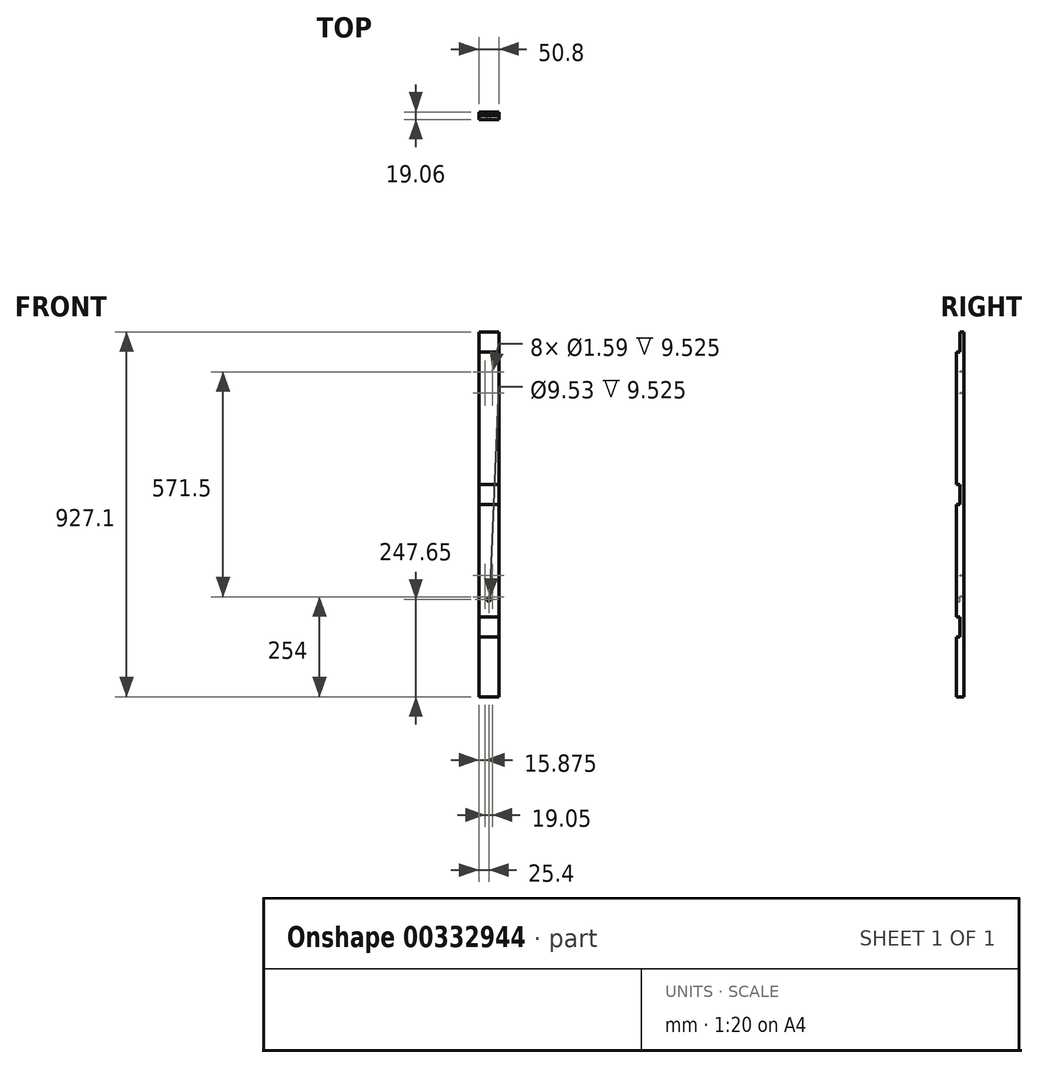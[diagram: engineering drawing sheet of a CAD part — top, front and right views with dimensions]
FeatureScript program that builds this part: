
annotation { "Feature Type Name" : "Feature", "Feature Type Description" : "" }
export const myFeature = defineFeature(function(context is Context, id is Id, definition is map)
    precondition{}
    {
        {
            var Q0;
            Q0=qCreatedBy(makeId("Top.planeOp"),FACE);
            var sketch = newSketch(context, id + "F0", { "sketchPlane" : qUnion([Q0])});
            skLineSegment(sketch, "E0.bottom", {"start": v(25.4, 9.53) * mm, "end": v(-25.4, 9.53) * mm});
            skLineSegment(sketch, "E0.top", {"start": v(25.4, -9.53) * mm, "end": v(-25.4, -9.53) * mm});
            skLineSegment(sketch, "E0.left", {"start": v(25.4, 9.53) * mm, "end": v(25.4, -9.52) * mm});
            skLineSegment(sketch, "E0.right", {"start": v(-25.4, 9.53) * mm, "end": v(-25.4, -9.53) * mm});
            skPoint(sketch, "E0.middle", {"position": v(0, 0) * mm});
            skSolve(sketch);
        }
        {
            var Q0;
            Q0=makeQuery(id+"F0.imprint","IMPRINT",FACE,{"disambiguationData":[TD([[makeQuery(id+"F0.imprint","IMPRINT",EDGE,{"derivedFrom":sQuery(id+"F0.wireOp",EDGE,"E0.bottom")}),1.0]])]});
            var Q1;
            Q1 = qSketchRegion(id + "F2", true);
            extrude(context, id + "F1", {"entities" : qUnion([Q0, Q1]), "depth" : 927.1 * mm});
        }
        {
            var Q0;
            Q0=qCreatedBy(makeId("Front.planeOp"),FACE);
            var sketch = newSketch(context, id + "F2", { "sketchPlane" : qUnion([Q0])});
            skLineSegment(sketch, "E1.bottom", {"start": v(-38.77, 152.4) * mm, "end": v(83.66, 152.4) * mm});
            skLineSegment(sketch, "E1.top", {"start": v(-38.77, 203.2) * mm, "end": v(83.66, 203.2) * mm});
            skLineSegment(sketch, "E1.left", {"start": v(-38.77, 152.4) * mm, "end": v(-38.77, 203.2) * mm});
            skLineSegment(sketch, "E1.right", {"start": v(83.66, 152.4) * mm, "end": v(83.66, 203.2) * mm});
            skLineSegment(sketch, "E2.bottom", {"start": v(-210.36, 876.3) * mm, "end": v(132.8, 876.3) * mm});
            skLineSegment(sketch, "E2.top", {"start": v(-210.36, 927.1) * mm, "end": v(132.8, 927.1) * mm});
            skLineSegment(sketch, "E2.left", {"start": v(-210.36, 876.3) * mm, "end": v(-210.36, 927.1) * mm});
            skLineSegment(sketch, "E2.right", {"start": v(132.8, 876.3) * mm, "end": v(132.8, 927.1) * mm});
            skLineSegment(sketch, "E3.bottom", {"start": v(-179.92, 539.75) * mm, "end": v(84.62, 539.75) * mm});
            skLineSegment(sketch, "E3.top", {"start": v(-179.92, 488.95) * mm, "end": v(84.62, 488.95) * mm});
            skLineSegment(sketch, "E3.left", {"start": v(-179.92, 539.75) * mm, "end": v(-179.92, 488.95) * mm});
            skLineSegment(sketch, "E3.right", {"start": v(84.62, 539.75) * mm, "end": v(84.62, 488.95) * mm});
            skSolve(sketch);
        }
        {
            var Q0;
            Q0=qSketchRegion(id+"F2",true);
            extrude(context, id + "F3", {"entities" : qUnion([Q0]), "operationType" : NewBodyOperationType.REMOVE, "depth" : 25.4 * mm});
        }
        {
            var Q0;
            Q0=qCreatedBy(makeId("Front.planeOp"),FACE);
            var sketch = newSketch(context, id + "F4", { "sketchPlane" : qUnion([Q0])});
            skCircle(sketch, "E4", {"center": v(9.53, 254) * mm, "radius": 0.8 * mm});
            skCircle(sketch, "E5", {"center": v(9.52, 307.98) * mm, "radius": 0.8 * mm});
            skCircle(sketch, "E6", {"center": v(9.52, 771.52) * mm, "radius": 0.8 * mm});
            skCircle(sketch, "E7", {"center": v(9.52, 825.5) * mm, "radius": 0.8 * mm});
            skLineSegment(sketch, "E8", {"start": v(0, 0) * mm, "end": v(0, 1192.46) * mm, "construction": true});
            skLineSegment(sketch, "E9.bottom", {"start": v(9.52, 254) * mm, "end": v(-9.52, 254) * mm, "construction": true});
            skLineSegment(sketch, "E9.top", {"start": v(9.52, 825.5) * mm, "end": v(-9.53, 825.5) * mm, "construction": true});
            skLineSegment(sketch, "E9.left", {"start": v(9.53, 254) * mm, "end": v(9.52, 825.5) * mm, "construction": true});
            skLineSegment(sketch, "E9.right", {"start": v(-9.53, 254) * mm, "end": v(-9.53, 825.5) * mm, "construction": true});
            skCircle(sketch, "E10", {"center": v(-9.53, 771.52) * mm, "radius": 0.8 * mm});
            skCircle(sketch, "E11", {"center": v(-9.53, 825.5) * mm, "radius": 0.8 * mm});
            skCircle(sketch, "E12", {"center": v(-9.53, 254) * mm, "radius": 0.8 * mm});
            skCircle(sketch, "E13", {"center": v(-9.53, 307.98) * mm, "radius": 0.8 * mm});
            skSolve(sketch);
        }
        {
            var Q0;
            Q0=qSketchRegion(id+"F4",true);
            extrude(context, id + "F5", {"entities" : qUnion([Q0]), "operationType" : NewBodyOperationType.REMOVE, "oppositeDirection" : true, "depth" : 25.4 * mm});
        }
        {
            var Q0;
            Q0=qCreatedBy(makeId("Front.planeOp"),FACE);
            var sketch = newSketch(context, id + "F6", { "sketchPlane" : qUnion([Q0])});
            skCircle(sketch, "E14", {"center": v(0, 247.65) * mm, "radius": 4.76 * mm});
            skSolve(sketch);
        }
        {
            var Q0;
            Q0 = qSketchRegion(id + "F6", true);
            extrude(context, id + "F7", {"entities" : qUnion([Q0]), "operationType" : NewBodyOperationType.REMOVE, "depth" : 25.4 * mm});
        }
    });
